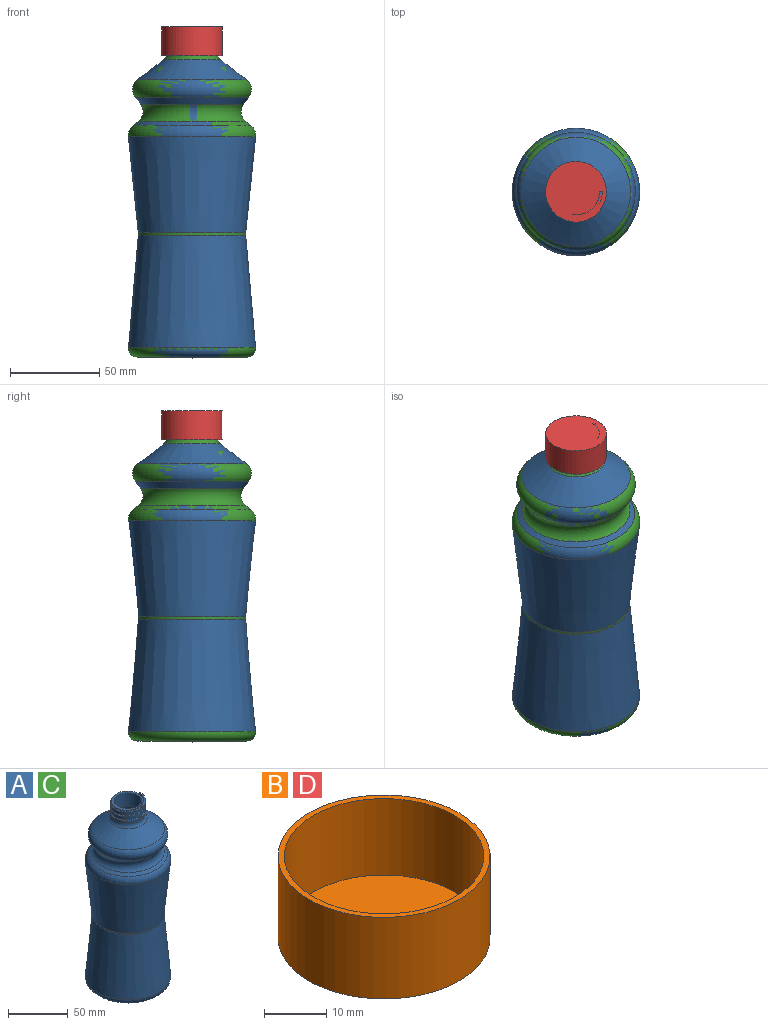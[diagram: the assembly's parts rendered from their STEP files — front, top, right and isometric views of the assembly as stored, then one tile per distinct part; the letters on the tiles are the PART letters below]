
ASSEMBLY  parts=4 mates=1
PART A: 35 faces, bbox 82.2x82.2x190.8 mm
  f0: cylinder r=14mm len=28mm, axis (0,0,1), area 216.1mm2, adj f3,f16,f32,f34
  f1: cylinder r=14mm len=28mm, axis (0,0,1), area 118.3mm2, adj f2,f4,f33
  f2: cylinder r=14mm len=28mm, axis (0,0,1), area 324.2mm2, adj f1,f3,f4,f32,f33
  f3: cylinder r=14mm len=28mm, axis (0,0,1), area 324.3mm2, adj f0,f2,f32,f33
  f4: plane 28.34x28.34mm, normal (0,0,1), area 178.2mm2, adj f1,f2,f17,f30,f31,f32,f33
  f5: cone r=14mm half-angle=52.8deg, axis (0,0,-1), area 2650.2mm2, adj f11,f16
  f6: cone r=36.03mm half-angle=37.2deg, axis (0,0,1), area 935.4mm2, adj f11,f12
  f7: cone r=24.6mm half-angle=52.8deg, axis (0,0,-1), area 675.6mm2, adj f12,f13
  f8: cone r=36.03mm half-angle=5.9deg, axis (0,0,1), area 11164.7mm2, adj f13,f14
  f9: cone r=30.01mm half-angle=5deg, axis (0,0,-1), area 13009mm2, adj f14,f15
  f10: cone r=36.03mm half-angle=89.1deg, axis (0,0,1), area 2953.8mm2, adj f15
  f11: torus R=26.22mm, axis (0,0,-1), area 2243mm2, adj f5,f6
  f12: torus R=34.41mm, axis (0,0,1), area 1945.8mm2, adj f6,f7
  f13: torus R=28.66mm, axis (0,0,-1), area 1568.5mm2, adj f7,f8
  f14: bspline ~60.12x60.09mm, area 251.1mm2, adj f8,f9
  f15: torus R=30.58mm, axis (0,0,-1), area 1748.2mm2, adj f9,f10
  f16: torus R=19mm, axis (0,0,1), area 425.1mm2, adj f0,f5
  f17: cylinder r=11.5mm len=23mm, axis (0,0,1), area 976.7mm2, adj f4,f29
  f18: cone r=12.49mm half-angle=52.8deg, axis (0,0,-1), area 2477.7mm2, adj f24,f29
  f19: cone r=34.04mm half-angle=37.2deg, axis (0,0,1), area 873.9mm2, adj f24,f25
  f20: cone r=23.09mm half-angle=52.8deg, axis (0,0,-1), area 643.2mm2, adj f25,f26
  f21: cone r=33.54mm half-angle=5.9deg, axis (0,0,1), area 10319.5mm2, adj f26,f27
  f22: cone r=27.52mm half-angle=5deg, axis (0,0,-1), area 12021.7mm2, adj f27,f28
  f23: cone r=35.99mm half-angle=89.1deg, axis (0,0,1), area 2946.1mm2, adj f28
  f24: torus R=26.22mm, axis (0,0,-1), area 1342.9mm2, adj f18,f19
  f25: torus R=34.41mm, axis (0,0,1), area 2431.6mm2, adj f19,f20
  f26: torus R=28.66mm, axis (0,0,-1), area 944.8mm2, adj f20,f21
  f27: offset ~66.72x66.72mm, area 312.5mm2, adj f21,f22
  f28: torus R=30.58mm, axis (0,0,-1), area 831.4mm2, adj f22,f23
  f29: torus R=19mm, axis (0,0,1), area 543.8mm2, adj f17,f18
  f30: plane 1.78x1.52mm, normal (0,1,0), area 1.5mm2, adj f4,f31,f32,f33
  f31: cylinder r=13.04mm len=19.85mm, axis (0,0,-1), area 21mm2, adj f4,f30,f33
  f32: bspline ~34.21x29.63mm, area 247.6mm2, adj f0,f2,f3,f4,f30,f33,f34
  f33: bspline ~34.21x29.63mm, area 275.4mm2, adj f1,f2,f3,f4,f30,f31,f32,f34
  f34: plane 0.82x0.82mm, normal (0,-1,0), area 0.3mm2, adj f0,f32,f33
PART B: 5 faces, bbox 34x34x16 mm
  f0: cylinder r=17mm len=34mm, axis (0,0,-1), area 1709mm2, adj f1,f2
  f1: plane 34x34mm, normal (0,0,1), area 103.7mm2, adj f0,f3
  f2: plane 34x34mm, normal (0,0,-1), area 907.9mm2, adj f0
  f3: cylinder r=16mm len=32mm, axis (0,0,-1), area 1508mm2, adj f1,f4
  f4: plane 32x32mm, normal (0,0,1), area 804.2mm2, adj f3
PART C: same geometry as A
PART D: same geometry as B
PLACE A t=(-46,-28.86,-12.49)mm
PLACE B t=(-46,-28.86,-12.49)mm
PLACE C t=(-46,-28.86,-12.49)mm fixed
PLACE D rot(axis=(0.71,0.71,0),180deg) t=(-46,-28.86,59.49)mm
MATE cylindrical D.f0 <-> C.f23  axis (0,0,-1) through (-46,-28.86,58.49)mm
